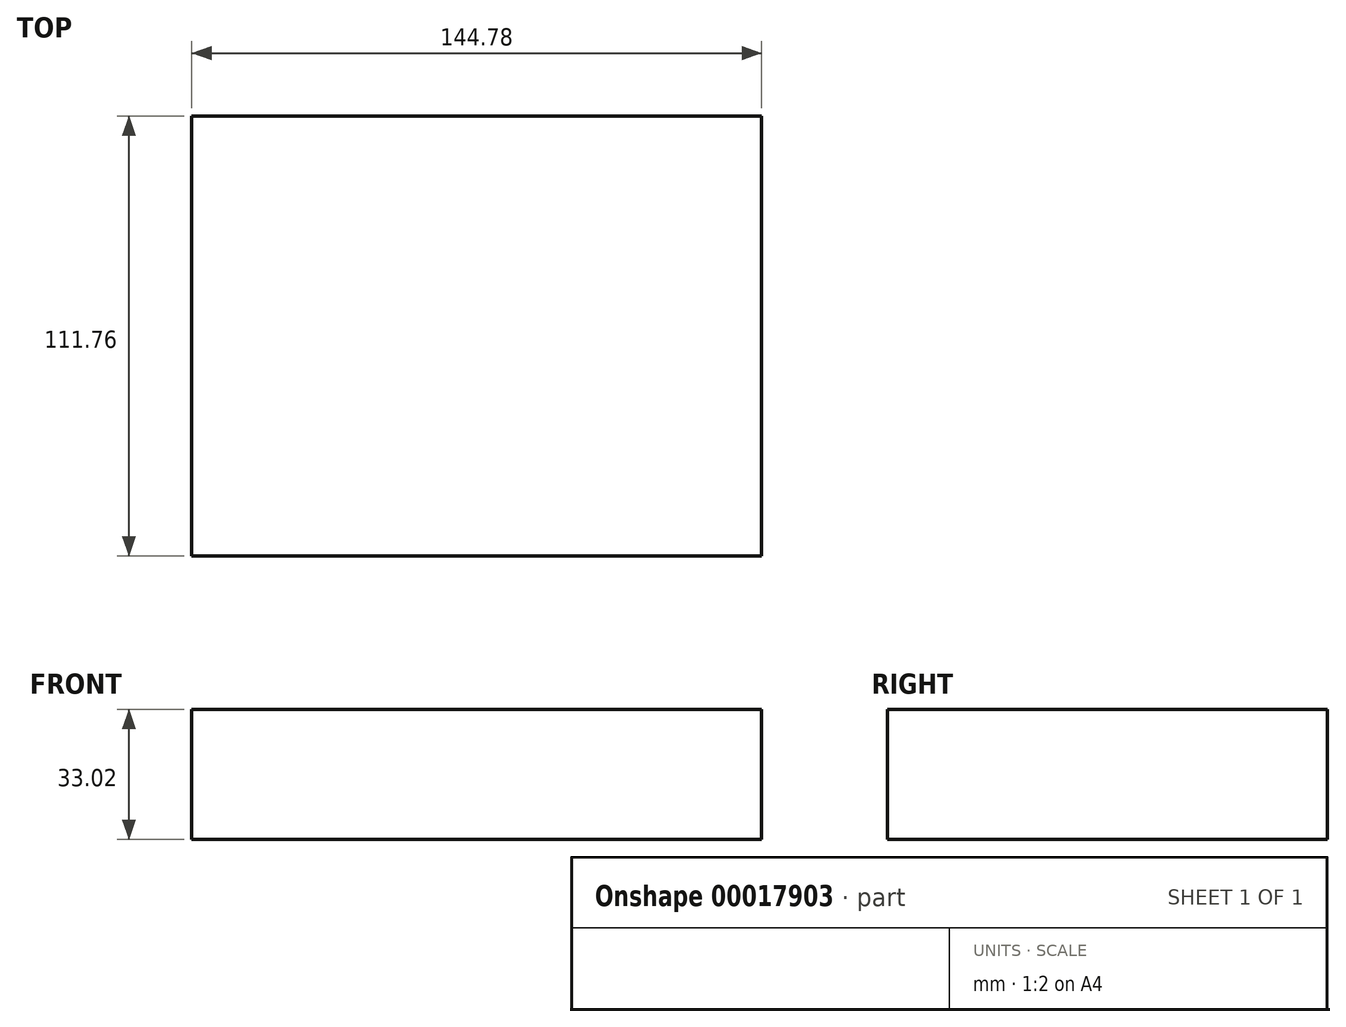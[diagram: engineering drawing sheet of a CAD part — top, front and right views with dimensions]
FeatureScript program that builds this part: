
annotation { "Feature Type Name" : "Feature", "Feature Type Description" : "" }
export const myFeature = defineFeature(function(context is Context, id is Id, definition is map)
    precondition{}
    {
        {
            var Q0;
            Q0=qCreatedBy(makeId("Top.planeOp"),FACE);
            var sketch = newSketch(context, id + "F0", { "sketchPlane" : qUnion([Q0])});
            skLineSegment(sketch, "E0.rect.bottom", {"start": v(-72.39, 55.88) * mm, "end": v(72.4, 55.88) * mm});
            skLineSegment(sketch, "E0.rect.top", {"start": v(-72.4, -55.88) * mm, "end": v(72.39, -55.88) * mm});
            skLineSegment(sketch, "E0.rect.left", {"start": v(-72.39, 55.88) * mm, "end": v(-72.4, -55.88) * mm});
            skLineSegment(sketch, "E0.rect.right", {"start": v(72.4, 55.88) * mm, "end": v(72.39, -55.88) * mm});
            skPoint(sketch, "E0.rect.middle", {"position": v(0, 0) * mm});
            skSolve(sketch);
        }
        {
            var Q0;
            Q0 = qSketchRegion(id + "F0", true);
            extrude(context, id + "F1", {"entities" : qUnion([Q0]), "depth" : 33.02 * mm});
        }
    });
